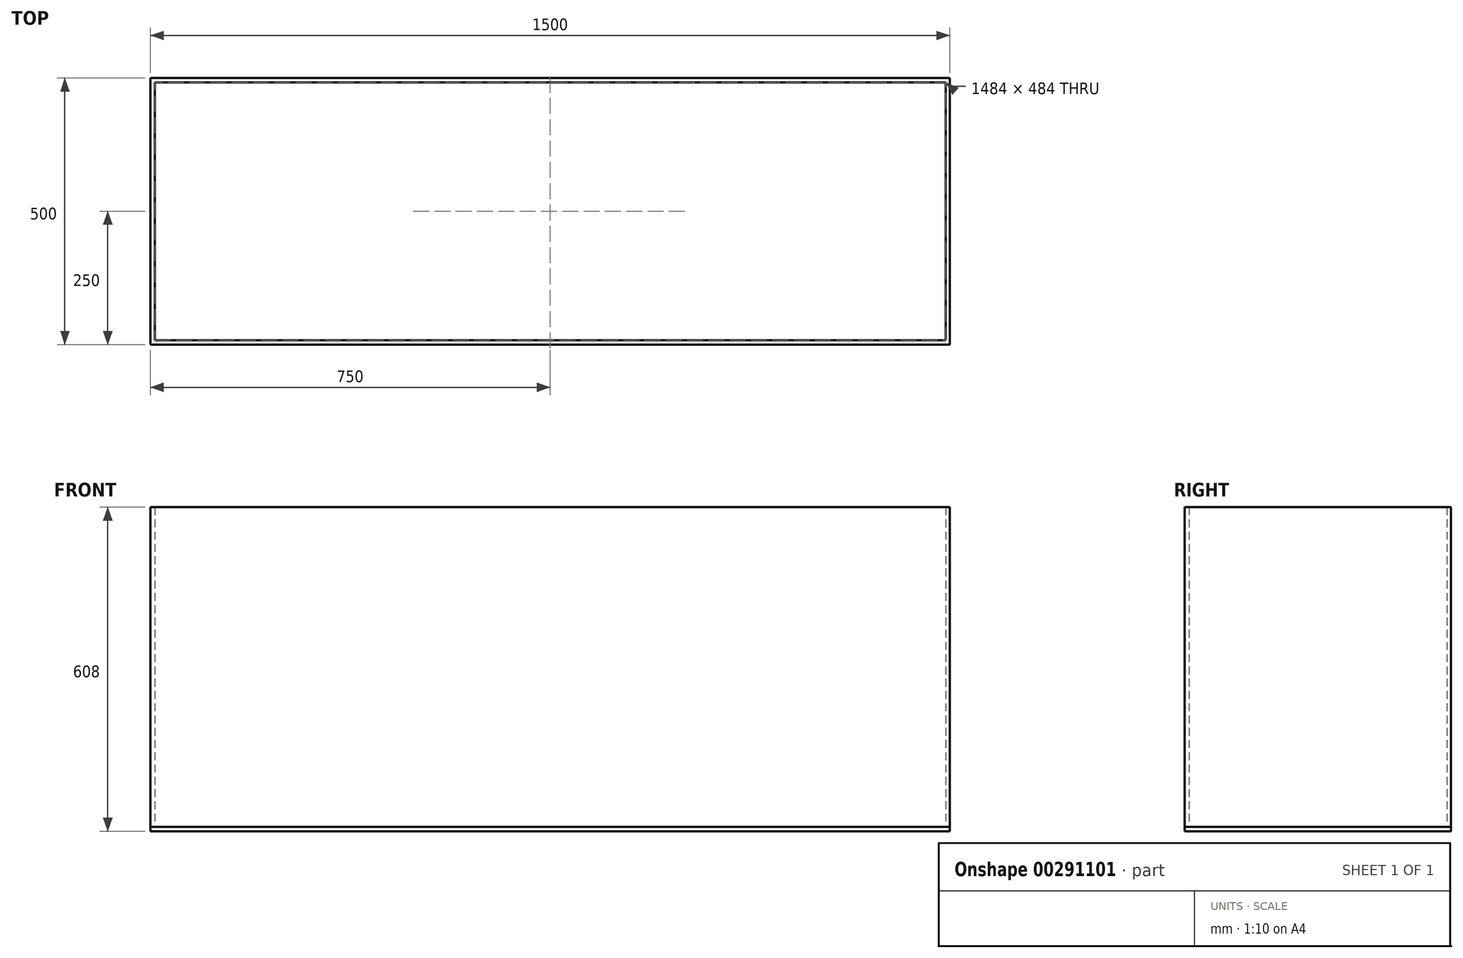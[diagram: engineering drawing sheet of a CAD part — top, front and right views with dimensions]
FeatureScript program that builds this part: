
annotation { "Feature Type Name" : "Feature", "Feature Type Description" : "" }
export const myFeature = defineFeature(function(context is Context, id is Id, definition is map)
    precondition{}
    {
        {
            var Q0;
            Q0=qCreatedBy(makeId("Top.planeOp"),FACE);
            var sketch = newSketch(context, id + "F0", { "sketchPlane" : qUnion([Q0])});
            skLineSegment(sketch, "E0.bottom", {"start": v(-750, 250) * mm, "end": v(750, 250) * mm});
            skLineSegment(sketch, "E0.top", {"start": v(-750, -250) * mm, "end": v(750, -250) * mm});
            skLineSegment(sketch, "E0.left", {"start": v(-750, 250) * mm, "end": v(-750, -250) * mm});
            skLineSegment(sketch, "E0.right", {"start": v(750, 250) * mm, "end": v(750, -250) * mm});
            skPoint(sketch, "E0.middle", {"position": v(0, 0) * mm});
            skLineSegment(sketch, "E1.bottom", {"start": v(-742, 242) * mm, "end": v(742, 242) * mm});
            skLineSegment(sketch, "E1.top", {"start": v(-742, -242) * mm, "end": v(742, -242) * mm});
            skLineSegment(sketch, "E1.left", {"start": v(-742, 242) * mm, "end": v(-742, -242) * mm});
            skLineSegment(sketch, "E1.right", {"start": v(742, 242) * mm, "end": v(742, -242) * mm});
            skSolve(sketch);
        }
        {
            var Q0;
            Q0=qSketchRegion(id+"F0",true);
            var Q1;
            Q1=makeQuery(id+"F0.imprint","IMPRINT",FACE,{"disambiguationData":[TD([[makeQuery(id+"F0.imprint","IMPRINT",EDGE,{"derivedFrom":sQuery(id+"F0.wireOp",EDGE,"E1.bottom")}),-1.0]])]});
            extrude(context, id + "F1", {"entities" : qUnion([Q0, Q1]), "oppositeDirection" : true, "depth" : 8 * mm});
        }
        {
            var Q0;
            Q0=qSketchRegion(id+"F0",true);
            extrude(context, id + "F2", {"entities" : qUnion([Q0]), "depth" : 600 * mm});
        }
    });
